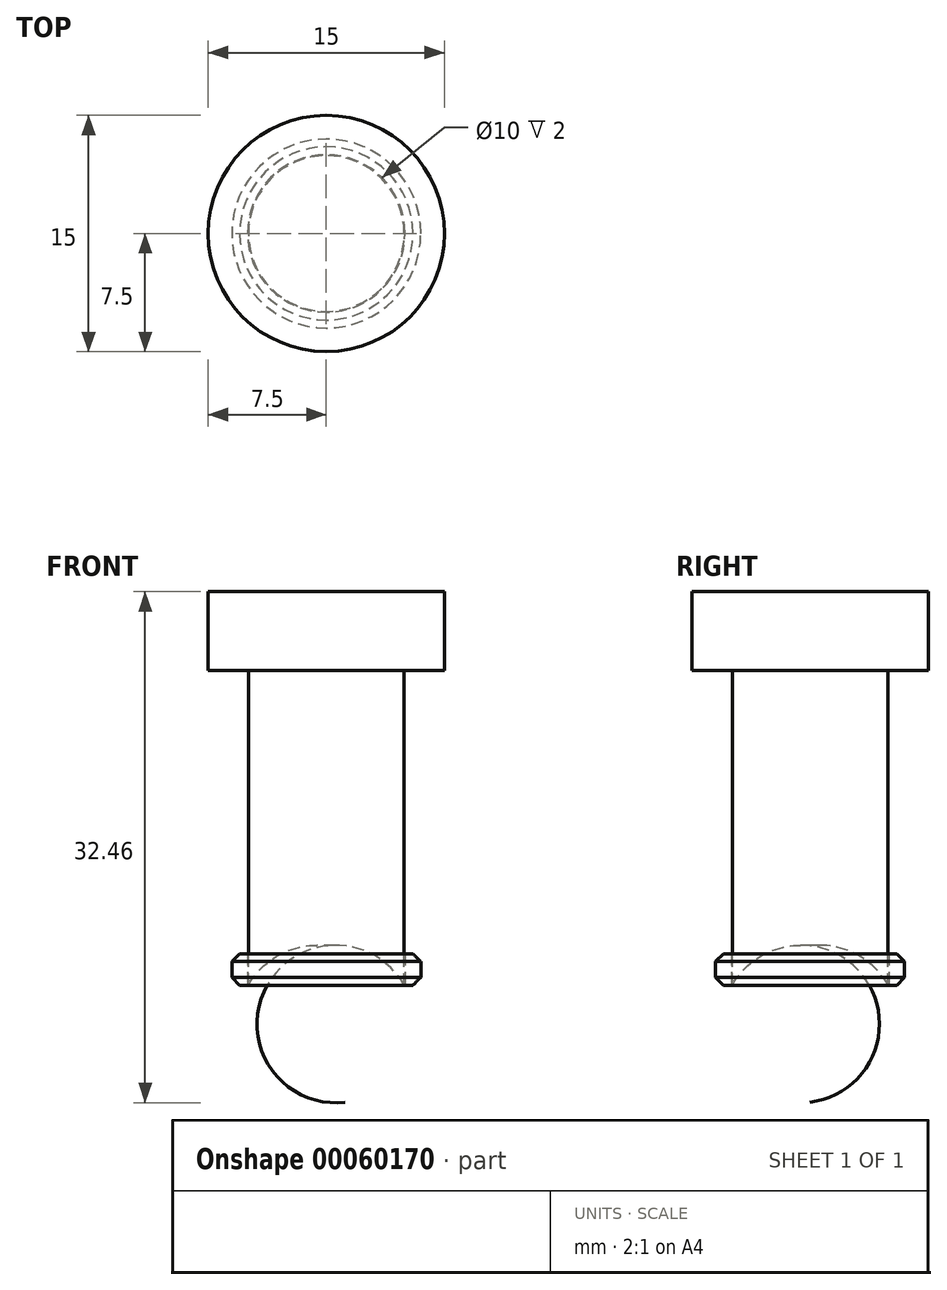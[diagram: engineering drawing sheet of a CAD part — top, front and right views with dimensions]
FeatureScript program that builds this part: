
annotation { "Feature Type Name" : "Feature", "Feature Type Description" : "" }
export const myFeature = defineFeature(function(context is Context, id is Id, definition is map)
    precondition{}
    {
        {
            var Q0;
            Q0=qCreatedBy(makeId("Front.planeOp"),FACE);
            var sketch = newSketch(context, id + "F0", { "sketchPlane" : qUnion([Q0])});
            skLineSegment(sketch, "E0", {"start": v(0, 0) * mm, "end": v(7.5, 0) * mm});
            skLineSegment(sketch, "E1", {"start": v(7.5, 0) * mm, "end": v(7.5, -5) * mm});
            skLineSegment(sketch, "E2", {"start": v(7.5, -5) * mm, "end": v(4.95, -5) * mm});
            skLineSegment(sketch, "E3", {"start": v(4.95, -5) * mm, "end": v(4.95, -25) * mm});
            skLineSegment(sketch, "E4", {"start": v(0, 0) * mm, "end": v(0, -22.5) * mm});
            skArc(sketch, "E5", {"start": v(4.95, -25) * mm, "mid": v(2.85, -23) * mm, "end": v(0, -22.5) * mm});
            skSolve(sketch);
        }
        {
            var Q0;
            Q0=makeQuery(id+"F0.imprint","IMPRINT",FACE,{"disambiguationData":[TD([[makeQuery(id+"F0.imprint","IMPRINT",EDGE,{"derivedFrom":sQuery(id+"F0.wireOp",EDGE,"E0")}),-1.0]])]});
            var Q1;
            Q1=sQuery(id+"F0.wireOp",EDGE,"E4");
            var Q2;
            Q2=sQuery(id+"F0.wireOp",EDGE,"E0");
            var Q3;
            Q3=sQuery(id+"F0.wireOp",EDGE,"E1");
            var Q4;
            Q4=sQuery(id+"F0.wireOp",EDGE,"E2");
            var Q5;
            Q5=sQuery(id+"F0.wireOp",EDGE,"E3");
            var Q6;
            Q6=sQuery(id+"F0.wireOp",EDGE,"E5");
            var Q7;
            Q7=sQuery(id+"F0.wireOp",EDGE,"E4");
            revolve(context, id + "F1", {"entities" : qUnion([Q0]), "surfaceEntities" : qUnion([Q1, Q2, Q3, Q4, Q5, Q6]), "axis" : qUnion([Q7]), "revolveType" : RevolveType.FULL});
        }
        {
            var Q0;
            Q0=qCreatedBy(makeId("Top.planeOp"),FACE);
            cPlane(context, id + "F2", {"entities" : qUnion([Q0]), "cplaneType" : CPlaneType.OFFSET, "offset" : 25 * mm, "oppositeDirection" : true, "width" : 150 * mm, "height" : 150 * mm});
        }
        {
            var Q0;
            Q0=qCreatedBy(id+"F2.planeOp",FACE);
            var sketch = newSketch(context, id + "F3", { "sketchPlane" : qUnion([Q0])});
            skCircle(sketch, "E6", {"center": v(0, 0) * mm, "radius": 5 * mm});
            skCircle(sketch, "E7", {"center": v(0, 0) * mm, "radius": 6 * mm});
            skSolve(sketch);
        }
        {
            var Q0;
            Q0 = qSketchRegion(id + "F3", true);
            extrude(context, id + "F4", {"entities" : qUnion([Q0]), "depth" : 2 * mm});
        }
        {
            var Q0;
            Q0=makeQuery(id+"F4.opExtrude","CAP_EDGE",EDGE,{"disambiguationData":[OSD([sQuery(id+"F3.wireOp",EDGE,"E7")])],"isStart":true});
            chamfer(context, id + "F5", {"entities" : qUnion([Q0]), "width" : 0.5 * mm, "tangentPropagation" : true});
        }
        {
            var Q0;
            Q0=makeQuery(id+"F4.opExtrude","CAP_EDGE",EDGE,{"disambiguationData":[OSD([sQuery(id+"F3.wireOp",EDGE,"E7")])],"isStart":false});
            chamfer(context, id + "F6", {"entities" : qUnion([Q0]), "width" : 0.5 * mm, "tangentPropagation" : true});
        }
    });
